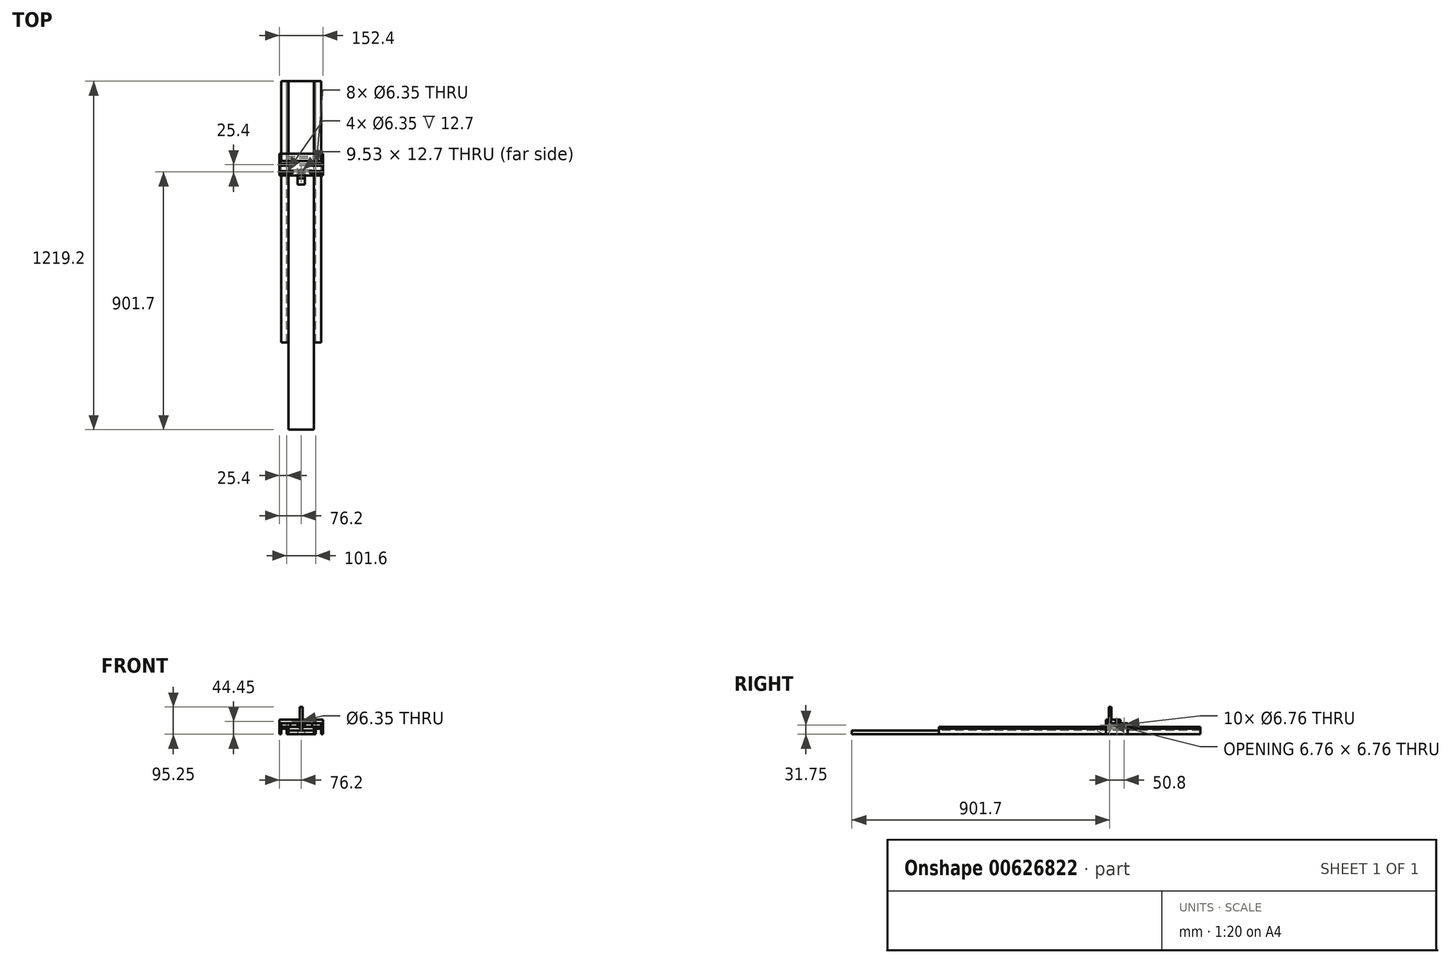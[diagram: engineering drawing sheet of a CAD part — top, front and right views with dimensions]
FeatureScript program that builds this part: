
annotation { "Feature Type Name" : "Feature", "Feature Type Description" : "" }
export const myFeature = defineFeature(function(context is Context, id is Id, definition is map)
    precondition{}
    {
        {
            var Q0;
            Q0=qCreatedBy(makeId("Top.planeOp"),FACE);
            var sketch = newSketch(context, id + "F0", { "sketchPlane" : qUnion([Q0])});
            skLineSegment(sketch, "E0.bottom", {"start": v(-44.45, 609.6) * mm, "end": v(44.45, 609.6) * mm});
            skLineSegment(sketch, "E0.top", {"start": v(-44.45, -609.6) * mm, "end": v(44.45, -609.6) * mm});
            skLineSegment(sketch, "E0.left", {"start": v(-44.45, 609.6) * mm, "end": v(-44.45, -609.6) * mm});
            skLineSegment(sketch, "E0.right", {"start": v(44.45, 609.6) * mm, "end": v(44.45, -609.6) * mm});
            skLineSegment(sketch, "E1", {"start": v(-44.45, 0) * mm, "end": v(44.45, 0) * mm, "construction": true});
            skSolve(sketch);
        }
        {
            var Q0;
            Q0 = qSketchRegion(id + "F0", true);
            extrude(context, id + "F1", {"entities" : qUnion([Q0]), "depth" : 12.7 * mm, "offsetDistance" : 25.4 * mm});
        }
        {
            var Q0;
            Q0=makeQuery(id+"F1.opExtrude","SWEPT_FACE",FACE,{"disambiguationData":[OSD([sQuery(id+"F0.wireOp",EDGE,"E0.bottom")])]});
            var sketch = newSketch(context, id + "F2", { "sketchPlane" : qUnion([Q0])});
            skLineSegment(sketch, "E2", {"start": v(-69.85, 25.4) * mm, "end": v(-44.45, 25.4) * mm});
            skLineSegment(sketch, "E3", {"start": v(-44.45, 25.4) * mm, "end": v(-44.45, 0) * mm});
            skLineSegment(sketch, "E4", {"start": v(-44.45, 0) * mm, "end": v(-50.8, 0) * mm});
            skLineSegment(sketch, "E5", {"start": v(-50.8, 0) * mm, "end": v(-50.8, 19.05) * mm});
            skLineSegment(sketch, "E6", {"start": v(-50.8, 19.05) * mm, "end": v(-69.85, 19.05) * mm});
            skLineSegment(sketch, "E7", {"start": v(-69.85, 19.05) * mm, "end": v(-69.85, 25.4) * mm});
            skLineSegment(sketch, "E8", {"start": v(0, 12.7) * mm, "end": v(0, 0) * mm, "construction": true});
            skLineSegment(sketch, "E9.MirrorCS", {"start": v(44.45, 25.4) * mm, "end": v(44.45, 0) * mm});
            skLineSegment(sketch, "E10.MirrorCS", {"start": v(44.45, 0) * mm, "end": v(50.8, 0) * mm});
            skLineSegment(sketch, "E11.MirrorCS", {"start": v(50.8, 0) * mm, "end": v(50.8, 19.05) * mm});
            skLineSegment(sketch, "E12.MirrorCS", {"start": v(50.8, 19.05) * mm, "end": v(69.85, 19.05) * mm});
            skLineSegment(sketch, "E13.MirrorCS", {"start": v(69.85, 25.4) * mm, "end": v(44.45, 25.4) * mm});
            skLineSegment(sketch, "E14.MirrorCS", {"start": v(69.85, 19.05) * mm, "end": v(69.85, 25.4) * mm});
            skSolve(sketch);
        }
        {
            var Q0;
            {var subQ4=sQuery(id+"F2.wireOp",EDGE,"E2");Q0=makeQuery(id+"F2.imprint","IMPRINT",FACE,{"disambiguationData":[TD([[makeQuery(id+"F2.imprint","IMPRINT",EDGE,{"derivedFrom":subQ4}),-1.0]])]});}
            extrude(context, id + "F3", {"entities" : qUnion([Q0]), "oppositeDirection" : true, "depth" : 914.4 * mm, "offsetDistance" : 25.4 * mm});
        }
        {
            var Q0;
            {var subQ0=sQuery(id+"F2.wireOp",EDGE,"E10.MirrorCS");Q0=makeQuery(id+"F2.imprint","IMPRINT",FACE,{"disambiguationData":[TD([[makeQuery(id+"F2.imprint","IMPRINT",EDGE,{"derivedFrom":subQ0}),1.0]])]});}
            extrude(context, id + "F4", {"entities" : qUnion([Q0]), "oppositeDirection" : true, "depth" : 914.4 * mm, "offsetDistance" : 25.4 * mm});
        }
        {
            var Q0;
            {var subQ4=sQuery(id+"F2.wireOp",EDGE,"E2");Q0=makeQuery(id+"F2.imprint","IMPRINT",FACE,{"disambiguationData":[TD([[makeQuery(id+"F2.imprint","IMPRINT",EDGE,{"derivedFrom":subQ4}),-1.0]])]});}
            cPlane(context, id + "F5", {"entities" : qUnion([Q0]), "cplaneType" : CPlaneType.OFFSET, "offset" : 254 * mm, "oppositeDirection" : true, "width" : 152.4 * mm, "height" : 152.4 * mm});
        }
        {
            var Q0;
            Q0=qCreatedBy(id+"F5.planeOp",FACE);
            var sketch = newSketch(context, id + "F6", { "sketchPlane" : qUnion([Q0])});
            skLineSegment(sketch, "E15.bottom", {"start": v(-69.85, 38.1) * mm, "end": v(69.85, 38.1) * mm});
            skLineSegment(sketch, "E15.top", {"start": v(-69.85, 25.4) * mm, "end": v(69.85, 25.4) * mm});
            skLineSegment(sketch, "E15.left", {"start": v(-69.85, 38.1) * mm, "end": v(-69.85, 25.4) * mm});
            skLineSegment(sketch, "E15.right", {"start": v(69.85, 38.1) * mm, "end": v(69.85, 25.4) * mm});
            skLineSegment(sketch, "E16.0", {"start": v(-44.45, 25.4) * mm, "end": v(-44.45, 0) * mm, "construction": true});
            skLineSegment(sketch, "E17.0", {"start": v(44.45, 25.4) * mm, "end": v(44.45, 0) * mm, "construction": true});
            skLineSegment(sketch, "E18", {"start": v(-44.45, 25.4) * mm, "end": v(44.45, 25.4) * mm, "construction": true});
            skPoint(sketch, "E19", {"position": v(0, 25.4) * mm});
            skLineSegment(sketch, "E20.bottom", {"start": v(-76.2, 38.1) * mm, "end": v(-69.85, 38.1) * mm});
            skLineSegment(sketch, "E20.top", {"start": v(-76.2, 0) * mm, "end": v(-69.85, 0) * mm});
            skLineSegment(sketch, "E20.left", {"start": v(-76.2, 38.1) * mm, "end": v(-76.2, 0) * mm});
            skLineSegment(sketch, "E20.right", {"start": v(-69.85, 38.1) * mm, "end": v(-69.85, 0) * mm});
            skLineSegment(sketch, "E21.MirrorCS", {"start": v(76.2, 38.1) * mm, "end": v(76.2, 0) * mm});
            skLineSegment(sketch, "E22.MirrorCS", {"start": v(76.2, 0) * mm, "end": v(69.85, 0) * mm});
            skLineSegment(sketch, "E23.MirrorCS", {"start": v(76.2, 38.1) * mm, "end": v(69.85, 38.1) * mm});
            skLineSegment(sketch, "E24.MirrorCS", {"start": v(69.85, 38.1) * mm, "end": v(69.85, 0) * mm});
            skSolve(sketch);
        }
        {
            var Q0;
            Q0=makeQuery(id+"F6.imprint","IMPRINT",FACE,{"disambiguationData":[TD([[makeQuery(id+"F6.imprint","IMPRINT",EDGE,{"derivedFrom":sQuery(id+"F6.wireOp",EDGE,"E15.bottom")}),-1.0]])]});
            extrude(context, id + "F7", {"entities" : qUnion([Q0]), "oppositeDirection" : true, "depth" : 76.2 * mm, "offsetDistance" : 25.4 * mm});
        }
        {
            var Q0;
            Q0=makeQuery(id+"F6.imprint","IMPRINT",FACE,{"disambiguationData":[TD([[makeQuery(id+"F6.imprint","IMPRINT",EDGE,{"derivedFrom":sQuery(id+"F6.wireOp",EDGE,"E15.left")}),-1.0]])]});
            extrude(context, id + "F8", {"entities" : qUnion([Q0]), "oppositeDirection" : true, "depth" : 76.2 * mm, "offsetDistance" : 25.4 * mm});
        }
        {
            var Q0;
            Q0=makeQuery(id+"F6.imprint","IMPRINT",FACE,{"disambiguationData":[TD([[makeQuery(id+"F6.imprint","IMPRINT",EDGE,{"derivedFrom":sQuery(id+"F6.wireOp",EDGE,"E15.right")}),1.0]])]});
            extrude(context, id + "F9", {"entities" : qUnion([Q0]), "oppositeDirection" : true, "depth" : 76.2 * mm, "offsetDistance" : 25.4 * mm});
        }
        {
            var Q0;
            Q0=makeQuery(id+"F9.opExtrude","SWEPT_FACE",FACE,{"disambiguationData":[OSD([sQuery(id+"F6.wireOp",EDGE,"E21.MirrorCS")])]});
            var sketch = newSketch(context, id + "F10", { "sketchPlane" : qUnion([Q0])});
            skCircle(sketch, "E25", {"center": v(-342.9, 31.75) * mm, "radius": 3.38 * mm});
            skCircle(sketch, "E26", {"center": v(-317.5, 31.75) * mm, "radius": 3.38 * mm});
            skCircle(sketch, "E27", {"center": v(-292.1, 31.75) * mm, "radius": 3.38 * mm});
            skLineSegment(sketch, "E28", {"start": v(-342.9, 31.75) * mm, "end": v(-292.1, 31.75) * mm, "construction": true});
            skSolve(sketch);
        }
        {
            var Q0;
            Q0 = qSketchRegion(id + "F10", true);
            extrude(context, id + "F11", {"entities" : qUnion([Q0]), "operationType" : NewBodyOperationType.REMOVE, "oppositeDirection" : true, "depth" : 762 * mm, "offsetDistance" : 25.4 * mm});
        }
        {
            var Q0;
            Q0=makeQuery(id+"F7.opExtrude","SWEPT_FACE",FACE,{"disambiguationData":[OSD([sQuery(id+"F6.wireOp",EDGE,"E15.right")])]});
            var sketch = newSketch(context, id + "F12", { "sketchPlane" : qUnion([Q0])});
            skPoint(sketch, "E29", {"position": v(-342.9, 31.75) * mm});
            skPoint(sketch, "E30", {"position": v(-317.5, 31.75) * mm});
            skPoint(sketch, "E31", {"position": v(-292.1, 31.75) * mm});
            skCircle(sketch, "E32", {"center": v(-342.9, 31.75) * mm, "radius": 3.18 * mm});
            skCircle(sketch, "E33", {"center": v(-317.5, 31.75) * mm, "radius": 3.18 * mm});
            skCircle(sketch, "E34", {"center": v(-292.1, 31.75) * mm, "radius": 3.18 * mm});
            skSolve(sketch);
        }
        {
            var Q0;
            Q0 = qSketchRegion(id + "F12", true);
            extrude(context, id + "F13", {"entities" : qUnion([Q0]), "operationType" : NewBodyOperationType.REMOVE, "oppositeDirection" : true, "depth" : 12.7 * mm, "offsetDistance" : 25.4 * mm});
        }
        {
            var Q0;
            Q0=makeQuery(id+"F7.opExtrude","SWEPT_FACE",FACE,{"disambiguationData":[OSD([sQuery(id+"F6.wireOp",EDGE,"E15.left")])]});
            var sketch = newSketch(context, id + "F14", { "sketchPlane" : qUnion([Q0])});
            skCircle(sketch, "E35", {"center": v(292.1, 31.75) * mm, "radius": 3.18 * mm});
            skCircle(sketch, "E36", {"center": v(317.5, 31.75) * mm, "radius": 3.18 * mm});
            skCircle(sketch, "E37", {"center": v(342.9, 31.75) * mm, "radius": 3.18 * mm});
            skSolve(sketch);
        }
        {
            var Q0;
            Q0 = qSketchRegion(id + "F14", true);
            extrude(context, id + "F15", {"entities" : qUnion([Q0]), "operationType" : NewBodyOperationType.REMOVE, "oppositeDirection" : true, "depth" : 12.7 * mm, "offsetDistance" : 25.4 * mm});
        }
        {
            var Q0;
            Q0=makeQuery(id+"F7.opExtrude","SWEPT_FACE",FACE,{"disambiguationData":[OSD([sQuery(id+"F6.wireOp",EDGE,"E15.bottom")])]});
            var sketch = newSketch(context, id + "F16", { "sketchPlane" : qUnion([Q0])});
            skLineSegment(sketch, "E38.bottom", {"start": v(-38.1, 298.45) * mm, "end": v(38.1, 298.45) * mm});
            skLineSegment(sketch, "E38.top", {"start": v(-38.1, 279.4) * mm, "end": v(38.1, 279.4) * mm});
            skLineSegment(sketch, "E38.left", {"start": v(-38.1, 298.45) * mm, "end": v(-38.1, 279.4) * mm});
            skLineSegment(sketch, "E38.right", {"start": v(38.1, 298.45) * mm, "end": v(38.1, 279.4) * mm});
            skLineSegment(sketch, "E39.0", {"start": v(69.85, 279.4) * mm, "end": v(-69.85, 279.4) * mm, "construction": true});
            skPoint(sketch, "E40", {"position": v(0, 279.4) * mm});
            skSolve(sketch);
        }
        {
            var Q0;
            Q0 = qSketchRegion(id + "F16", true);
            extrude(context, id + "F17", {"entities" : qUnion([Q0]), "operationType" : NewBodyOperationType.REMOVE, "oppositeDirection" : true, "depth" : 25.4 * mm, "offsetDistance" : 25.4 * mm});
        }
        {
            var Q0;
            Q0=makeQuery(id+"F7.opExtrude","SWEPT_FACE",FACE,{"disambiguationData":[OSD([sQuery(id+"F6.wireOp",EDGE,"E15.bottom")])]});
            var sketch = newSketch(context, id + "F18", { "sketchPlane" : qUnion([Q0])});
            skLineSegment(sketch, "E41.bottom", {"start": v(-50.8, 279.4) * mm, "end": v(50.8, 279.4) * mm, "construction": true});
            skLineSegment(sketch, "E41.top", {"start": v(-50.8, 317.5) * mm, "end": v(50.8, 317.5) * mm, "construction": true});
            skLineSegment(sketch, "E41.left", {"start": v(-50.8, 279.4) * mm, "end": v(-50.8, 317.5) * mm, "construction": true});
            skLineSegment(sketch, "E41.right", {"start": v(50.8, 279.4) * mm, "end": v(50.8, 317.5) * mm, "construction": true});
            skLineSegment(sketch, "E42", {"start": v(-38.1, 279.4) * mm, "end": v(38.1, 279.4) * mm, "construction": true});
            skPoint(sketch, "E43", {"position": v(0, 279.4) * mm});
            skPoint(sketch, "E44", {"position": v(-50.8, 292.1) * mm});
            skPoint(sketch, "E45", {"position": v(50.8, 292.1) * mm});
            skCircle(sketch, "E46", {"center": v(-50.8, 317.5) * mm, "radius": 3.18 * mm});
            skCircle(sketch, "E47", {"center": v(50.8, 317.5) * mm, "radius": 3.18 * mm});
            skCircle(sketch, "E48", {"center": v(50.8, 292.1) * mm, "radius": 3.18 * mm});
            skCircle(sketch, "E49", {"center": v(-50.8, 292.1) * mm, "radius": 3.18 * mm});
            skSolve(sketch);
        }
        {
            var Q0;
            Q0=makeQuery(id+"F7.opExtrude","SWEPT_FACE",FACE,{"disambiguationData":[OSD([sQuery(id+"F6.wireOp",EDGE,"E15.bottom")])]});
            var sketch = newSketch(context, id + "F19", { "sketchPlane" : qUnion([Q0])});
            skLineSegment(sketch, "E50.bottom", {"start": v(-76.2, 330.2) * mm, "end": v(76.2, 330.2) * mm});
            skLineSegment(sketch, "E50.top", {"start": v(-76.2, 279.4) * mm, "end": v(76.2, 279.4) * mm});
            skLineSegment(sketch, "E50.left", {"start": v(-76.2, 330.2) * mm, "end": v(-76.2, 320.88) * mm});
            skLineSegment(sketch, "E50.right", {"start": v(76.2, 330.2) * mm, "end": v(76.2, 320.88) * mm});
            skLineSegment(sketch, "E51.bottom", {"start": v(-4.76, 285.75) * mm, "end": v(4.76, 285.75) * mm});
            skLineSegment(sketch, "E51.top", {"start": v(-4.76, 298.45) * mm, "end": v(4.76, 298.45) * mm});
            skLineSegment(sketch, "E51.left", {"start": v(4.76, 298.45) * mm, "end": v(4.76, 285.75) * mm});
            skLineSegment(sketch, "E51.right", {"start": v(-4.76, 298.45) * mm, "end": v(-4.76, 285.75) * mm});
            skLineSegment(sketch, "E52", {"start": v(-38.1, 279.4) * mm, "end": v(38.1, 279.4) * mm, "construction": true});
            skPoint(sketch, "E53", {"position": v(0, 279.4) * mm});
            skLineSegment(sketch, "E54", {"start": v(-38.1, 298.45) * mm, "end": v(38.1, 298.45) * mm, "construction": true});
            skPoint(sketch, "E55", {"position": v(0, 298.45) * mm});
            skArc(sketch, "E56", {"start": v(-31.75, 288.72) * mm, "mid": v(-28.37, 292.1) * mm, "end": v(-31.75, 295.48) * mm});
            skLineSegment(sketch, "E57", {"start": v(-76.2, 295.48) * mm, "end": v(-31.75, 295.48) * mm});
            skLineSegment(sketch, "E58", {"start": v(-76.2, 288.72) * mm, "end": v(-31.75, 288.72) * mm});
            skLineSegment(sketch, "E59", {"start": v(-76.2, 304.8) * mm, "end": v(76.2, 304.8) * mm, "construction": true});
            skLineSegment(sketch, "E60", {"start": v(0, 330.2) * mm, "end": v(0, 279.4) * mm, "construction": true});
            skLineSegment(sketch, "E61.MirrorCS", {"start": v(-76.2, 314.12) * mm, "end": v(-31.75, 314.12) * mm});
            skLineSegment(sketch, "E62.MirrorCS", {"start": v(-76.2, 320.88) * mm, "end": v(-31.75, 320.88) * mm});
            skArc(sketch, "E63.MirrorCS", {"start": v(-31.75, 320.88) * mm, "mid": v(-28.37, 317.5) * mm, "end": v(-31.75, 314.12) * mm});
            skArc(sketch, "E64.MirrorCS", {"start": v(31.75, 288.72) * mm, "mid": v(28.37, 292.1) * mm, "end": v(31.75, 295.48) * mm});
            skLineSegment(sketch, "E65.MirrorCS", {"start": v(76.2, 288.72) * mm, "end": v(31.75, 288.72) * mm});
            skLineSegment(sketch, "E66.MirrorCS", {"start": v(76.2, 295.48) * mm, "end": v(31.75, 295.48) * mm});
            skLineSegment(sketch, "E67.MirrorCS", {"start": v(76.2, 320.88) * mm, "end": v(31.75, 320.88) * mm});
            skLineSegment(sketch, "E68.MirrorCS", {"start": v(76.2, 314.12) * mm, "end": v(31.75, 314.12) * mm});
            skArc(sketch, "E69.MirrorCS", {"start": v(31.75, 320.88) * mm, "mid": v(28.37, 317.5) * mm, "end": v(31.75, 314.12) * mm});
            skPoint(sketch, "E70.orphan", {"position": v(-116.46, 320.88) * mm});
            skPoint(sketch, "E71.orphan", {"position": v(-141.45, 295.48) * mm});
            skPoint(sketch, "E72.orphan", {"position": v(-116.46, 288.72) * mm});
            skPoint(sketch, "E73.orphan", {"position": v(-141.45, 314.12) * mm});
            skPoint(sketch, "E74.orphan", {"position": v(116.46, 320.88) * mm});
            skPoint(sketch, "E75.orphan", {"position": v(141.45, 314.12) * mm});
            skPoint(sketch, "E76.orphan", {"position": v(141.45, 295.48) * mm});
            skPoint(sketch, "E77.orphan", {"position": v(116.46, 288.72) * mm});
            skLineSegment(sketch, "E78.trimOffspring", {"start": v(76.2, 288.72) * mm, "end": v(76.2, 279.4) * mm});
            skLineSegment(sketch, "E79.trimOffspring", {"start": v(76.2, 314.12) * mm, "end": v(76.2, 295.48) * mm});
            skLineSegment(sketch, "E80.trimOffspring", {"start": v(-76.2, 314.12) * mm, "end": v(-76.2, 295.48) * mm});
            skLineSegment(sketch, "E81.trimOffspring", {"start": v(-76.2, 288.72) * mm, "end": v(-76.2, 279.4) * mm});
            skSolve(sketch);
        }
        {
            var Q0;
            Q0 = qSketchRegion(id + "F19", true);
            extrude(context, id + "F20", {"entities" : qUnion([Q0]), "depth" : 12.7 * mm, "offsetDistance" : 25.4 * mm});
        }
        {
            var Q0;
            Q0=makeQuery(id+"F20.opExtrude","SWEPT_FACE",FACE,{"disambiguationData":[OSD([sQuery(id+"F19.wireOp",EDGE,"E50.top")])]});
            var sketch = newSketch(context, id + "F21", { "sketchPlane" : qUnion([Q0])});
            skLineSegment(sketch, "E82", {"start": v(-76.2, 44.45) * mm, "end": v(76.2, 44.45) * mm, "construction": true});
            skLineSegment(sketch, "E83", {"start": v(0, 50.8) * mm, "end": v(0, 38.1) * mm, "construction": true});
            skPoint(sketch, "E84", {"position": v(0, 44.45) * mm});
            skCircle(sketch, "E85", {"center": v(0, 44.45) * mm, "radius": 3.18 * mm});
            skSolve(sketch);
        }
        {
            var Q0;
            Q0 = qSketchRegion(id + "F21", true);
            extrude(context, id + "F22", {"entities" : qUnion([Q0]), "operationType" : NewBodyOperationType.REMOVE, "oppositeDirection" : true, "depth" : 12.7 * mm, "offsetDistance" : 25.4 * mm});
        }
        {
            var Q0;
            Q0 = qSketchRegion(id + "F18", true);
            extrude(context, id + "F23", {"entities" : qUnion([Q0]), "operationType" : NewBodyOperationType.REMOVE, "oppositeDirection" : true, "depth" : 25.4 * mm, "offsetDistance" : 25.4 * mm});
        }
        {
            var Q0;
            Q0=makeQuery(id+"F20.opExtrude","CAP_FACE",FACE,{"disambiguationData":[OSD([sQuery(id+"F19.wireOp",EDGE,"E50.bottom"),sQuery(id+"F19.wireOp",EDGE,"E50.top"),sQuery(id+"F19.wireOp",EDGE,"E50.left"),sQuery(id+"F19.wireOp",EDGE,"E50.right"),sQuery(id+"F19.wireOp",EDGE,"E51.bottom"),sQuery(id+"F19.wireOp",EDGE,"E51.top"),sQuery(id+"F19.wireOp",EDGE,"E51.left"),sQuery(id+"F19.wireOp",EDGE,"E51.right"),sQuery(id+"F19.wireOp",EDGE,"E56"),sQuery(id+"F19.wireOp",EDGE,"E57"),sQuery(id+"F19.wireOp",EDGE,"E58"),sQuery(id+"F19.wireOp",EDGE,"E61.MirrorCS"),sQuery(id+"F19.wireOp",EDGE,"E62.MirrorCS"),sQuery(id+"F19.wireOp",EDGE,"E63.MirrorCS"),sQuery(id+"F19.wireOp",EDGE,"E64.MirrorCS"),sQuery(id+"F19.wireOp",EDGE,"E65.MirrorCS"),sQuery(id+"F19.wireOp",EDGE,"E66.MirrorCS"),sQuery(id+"F19.wireOp",EDGE,"E67.MirrorCS"),sQuery(id+"F19.wireOp",EDGE,"E68.MirrorCS"),sQuery(id+"F19.wireOp",EDGE,"E69.MirrorCS"),sQuery(id+"F19.wireOp",EDGE,"E78.trimOffspring"),sQuery(id+"F19.wireOp",EDGE,"E79.trimOffspring"),sQuery(id+"F19.wireOp",EDGE,"E80.trimOffspring"),sQuery(id+"F19.wireOp",EDGE,"E81.trimOffspring")])],"isStart":false});
            var sketch = newSketch(context, id + "F24", { "sketchPlane" : qUnion([Q0])});
            skLineSegment(sketch, "E86.bottom", {"start": v(-4.76, 298.45) * mm, "end": v(4.76, 298.45) * mm});
            skLineSegment(sketch, "E86.top", {"start": v(-4.76, 288.93) * mm, "end": v(4.76, 288.93) * mm});
            skLineSegment(sketch, "E86.left", {"start": v(-4.76, 298.45) * mm, "end": v(-4.76, 288.93) * mm});
            skLineSegment(sketch, "E86.right", {"start": v(4.76, 298.45) * mm, "end": v(4.76, 288.93) * mm});
            skSolve(sketch);
        }
        {
            var Q0;
            Q0 = qSketchRegion(id + "F24", true);
            extrude(context, id + "F25", {"entities" : qUnion([Q0]), "depth" : 44.45 * mm, "offsetDistance" : 25.4 * mm, "hasSecondDirection" : true, "secondDirectionOppositeDirection" : true, "secondDirectionDepth" : 31.75 * mm});
        }
        {
            var Q0;
            Q0=makeQuery(id+"F25.opExtrude","CAP_EDGE",EDGE,{"disambiguationData":[OSD([sQuery(id+"F24.wireOp",EDGE,"E86.bottom")])],"isStart":true});
            cPlane(context, id + "F26", {"entities" : qUnion([Q0]), "cplaneType" : CPlaneType.LINE_ANGLE, "offset" : 25.4 * mm, "angle" : 30 * degree, "oppositeDirection" : true, "width" : 152.4 * mm, "height" : 152.4 * mm});
        }
        {
            var Q0;
            Q0=qCreatedBy(id+"F26.planeOp",FACE);
            var sketch = newSketch(context, id + "F27", { "sketchPlane" : qUnion([Q0])});
            skLineSegment(sketch, "E87", {"start": v(0, 140.32) * mm, "end": v(0, 165.72) * mm, "construction": true});
            skLineSegment(sketch, "E88", {"start": v(12.7, 134.96) * mm, "end": v(-12.7, 134.96) * mm});
            skArc(sketch, "E89.MirrorCS", {"start": v(12.7, 178.42) * mm, "mid": v(0, 165.72) * mm, "end": v(-12.7, 178.42) * mm});
            skLineSegment(sketch, "E90", {"start": v(-12.7, 178.42) * mm, "end": v(12.7, 178.42) * mm, "construction": true});
            skLineSegment(sketch, "E91", {"start": v(-12.7, 134.96) * mm, "end": v(-12.7, 178.42) * mm});
            skLineSegment(sketch, "E92", {"start": v(12.7, 178.42) * mm, "end": v(12.7, 134.96) * mm});
            skSolve(sketch);
        }
        {
            var Q0;
            Q0 = qSketchRegion(id + "F27", true);
            extrude(context, id + "F28", {"entities" : qUnion([Q0]), "operationType" : NewBodyOperationType.REMOVE, "oppositeDirection" : true, "depth" : 67.82 * mm, "offsetDistance" : 25.4 * mm});
        }
    });
